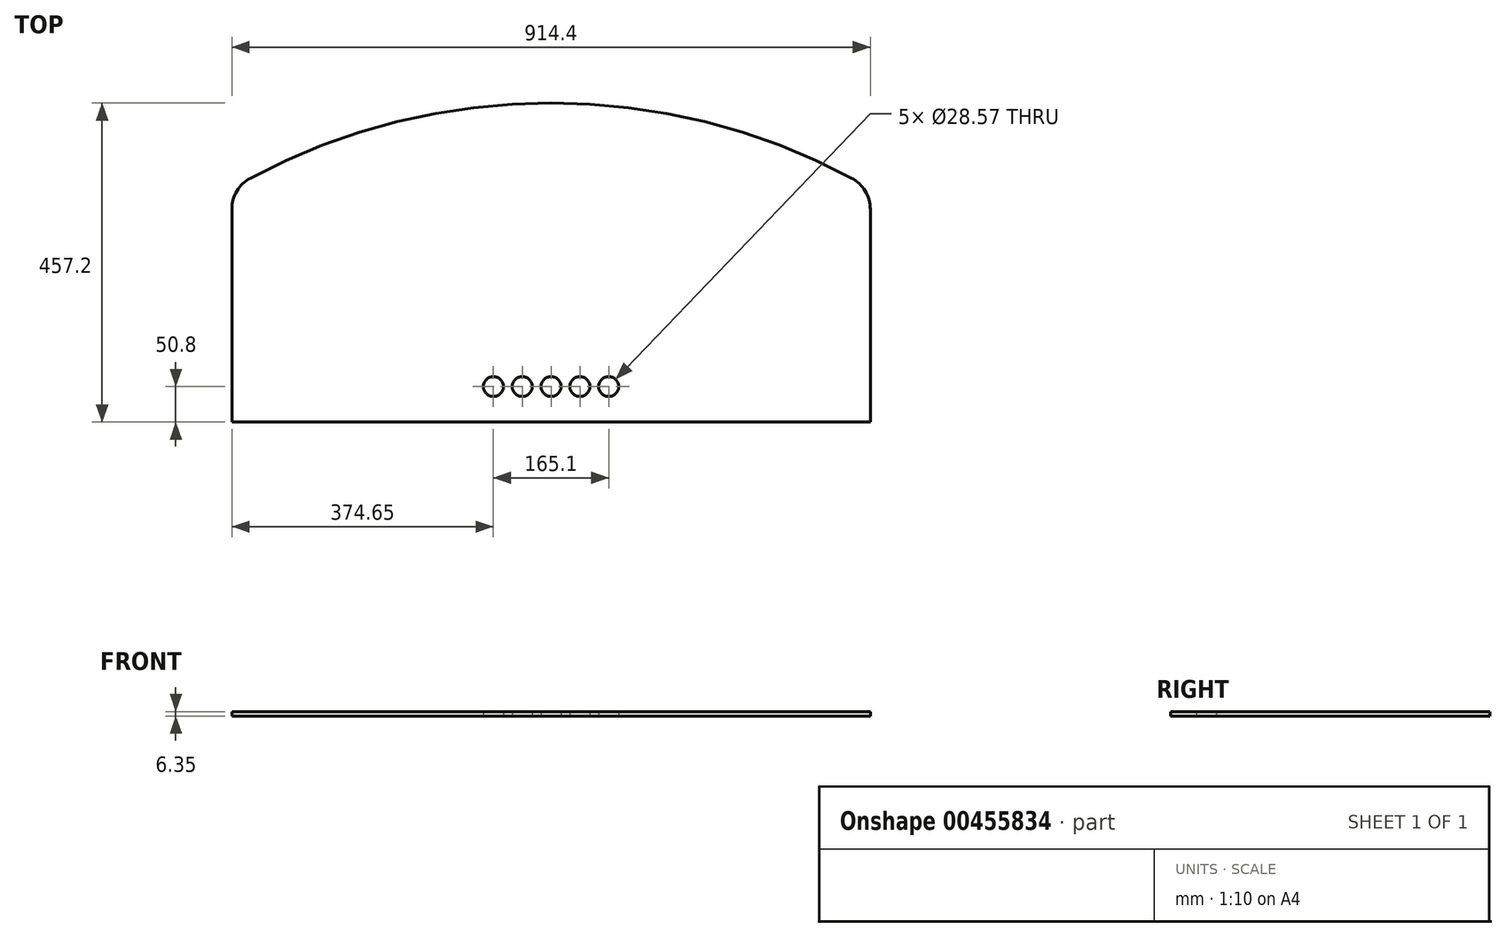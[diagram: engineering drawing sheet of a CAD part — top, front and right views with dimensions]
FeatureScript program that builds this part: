
annotation { "Feature Type Name" : "Feature", "Feature Type Description" : "" }
export const myFeature = defineFeature(function(context is Context, id is Id, definition is map)
    precondition{}
    {
        {
            var Q0;
            Q0=qCreatedBy(makeId("Top.planeOp"),FACE);
            var sketch = newSketch(context, id + "F0", { "sketchPlane" : qUnion([Q0])});
            skLineSegment(sketch, "E0.bottom", {"start": v(0, 0) * mm, "end": v(-914.4, 0) * mm});
            skLineSegment(sketch, "E0.left", {"start": v(0, 0) * mm, "end": v(0, 304.8) * mm});
            skLineSegment(sketch, "E0.right", {"start": v(-914.4, 0) * mm, "end": v(-914.4, 304.8) * mm});
            skArc(sketch, "E1", {"start": v(-26.9, 349.62) * mm, "mid": v(-457.2, 457.2) * mm, "end": v(-887.5, 349.62) * mm});
            skArc(sketch, "E2.filletArc", {"start": v(-887.5, 349.62) * mm, "mid": v(-907.16, 330.94) * mm, "end": v(-914.4, 304.8) * mm});
            skArc(sketch, "E3.filletArc", {"start": v(0, 304.8) * mm, "mid": v(-7.24, 330.94) * mm, "end": v(-26.9, 349.62) * mm});
            skLineSegment(sketch, "E4", {"start": v(-457.2, 0) * mm, "end": v(-457.2, 457.2) * mm, "construction": true});
            skSolve(sketch);
        }
        {
            var Q0;
            Q0=makeQuery(id+"F0.imprint","IMPRINT",FACE,{"disambiguationData":[TD([[makeQuery(id+"F0.imprint","IMPRINT",EDGE,{"derivedFrom":sQuery(id+"F0.wireOp",EDGE,"E0.bottom")}),-1.0]])]});
            var Q1;
            Q1 = qSketchRegion(id + "F2", true);
            extrude(context, id + "F1", {"entities" : qUnion([Q0, Q1]), "depth" : 6.35 * mm});
        }
        {
            var Q0;
            Q0=qCreatedBy(makeId("Top.planeOp"),FACE);
            var sketch = newSketch(context, id + "F2", { "sketchPlane" : qUnion([Q0])});
            skLineSegment(sketch, "E5", {"start": v(0, 0) * mm, "end": v(-914.4, 0) * mm, "construction": true});
            skLineSegment(sketch, "E6", {"start": v(-457.2, 0) * mm, "end": v(-457.2, 457.2) * mm, "construction": true});
            skPoint(sketch, "E6.endSnap0", {"position": v(-457.2, 0) * mm});
            skLineSegment(sketch, "E7", {"start": v(0, 0) * mm, "end": v(0, 304.8) * mm, "construction": true});
            skLineSegment(sketch, "E8", {"start": v(0, 304.8) * mm, "end": v(-914.4, 304.8) * mm, "construction": true});
            skLineSegment(sketch, "E9", {"start": v(0, 0) * mm, "end": v(0, 50.8) * mm, "construction": true});
            skLineSegment(sketch, "E10", {"start": v(0, 50.8) * mm, "end": v(-914.4, 50.8) * mm, "construction": true});
            skPoint(sketch, "E11", {"position": v(-457.2, 50.8) * mm});
            skPoint(sketch, "E12", {"position": v(-415.93, 50.8) * mm});
            skPoint(sketch, "E13", {"position": v(-374.65, 50.8) * mm});
            skPoint(sketch, "E14", {"position": v(-498.48, 50.8) * mm});
            skPoint(sketch, "E15", {"position": v(-539.75, 50.8) * mm});
            skLineSegment(sketch, "E16", {"start": v(-914.4, 304.8) * mm, "end": v(-457.2, 457.2) * mm, "construction": true});
            skSolve(sketch);
        }
        {
            var Q0;
            Q0=sQuery(id+"F2.wireOp",VERTEX,"E12");
            var Q1;
            Q1=sQuery(id+"F2.wireOp",VERTEX,"E13");
            var Q2;
            Q2=sQuery(id+"F2.wireOp",VERTEX,"E11");
            var Q3;
            Q3=sQuery(id+"F2.wireOp",VERTEX,"E14");
            var Q4;
            Q4=sQuery(id+"F2.wireOp",VERTEX,"E15");
            var Q5;
            Q5=makeQuery(id+"F1.opExtrude","SWEPT_BODY",BODY,{"disambiguationData":[OSD([sQuery(id+"F0.wireOp",EDGE,"E0.bottom"),sQuery(id+"F0.wireOp",EDGE,"E0.left"),sQuery(id+"F0.wireOp",EDGE,"E0.right"),sQuery(id+"F0.wireOp",EDGE,"E1"),sQuery(id+"F0.wireOp",EDGE,"E2.filletArc"),sQuery(id+"F0.wireOp",EDGE,"E3.filletArc")])]});
            hole(context, id + "F3", {"style" : HoleStyle.SIMPLE, "endStyle" : HoleEndStyle.THROUGH, "oppositeDirection" : true, "holeDiameter" : 28.57 * mm, "locations" : qUnion([Q0, Q1, Q2, Q3, Q4]), "scope" : qUnion([Q5]), "tappedDepth" : 12.7 * mm, "tapClearance" : 3});
        }
    });
